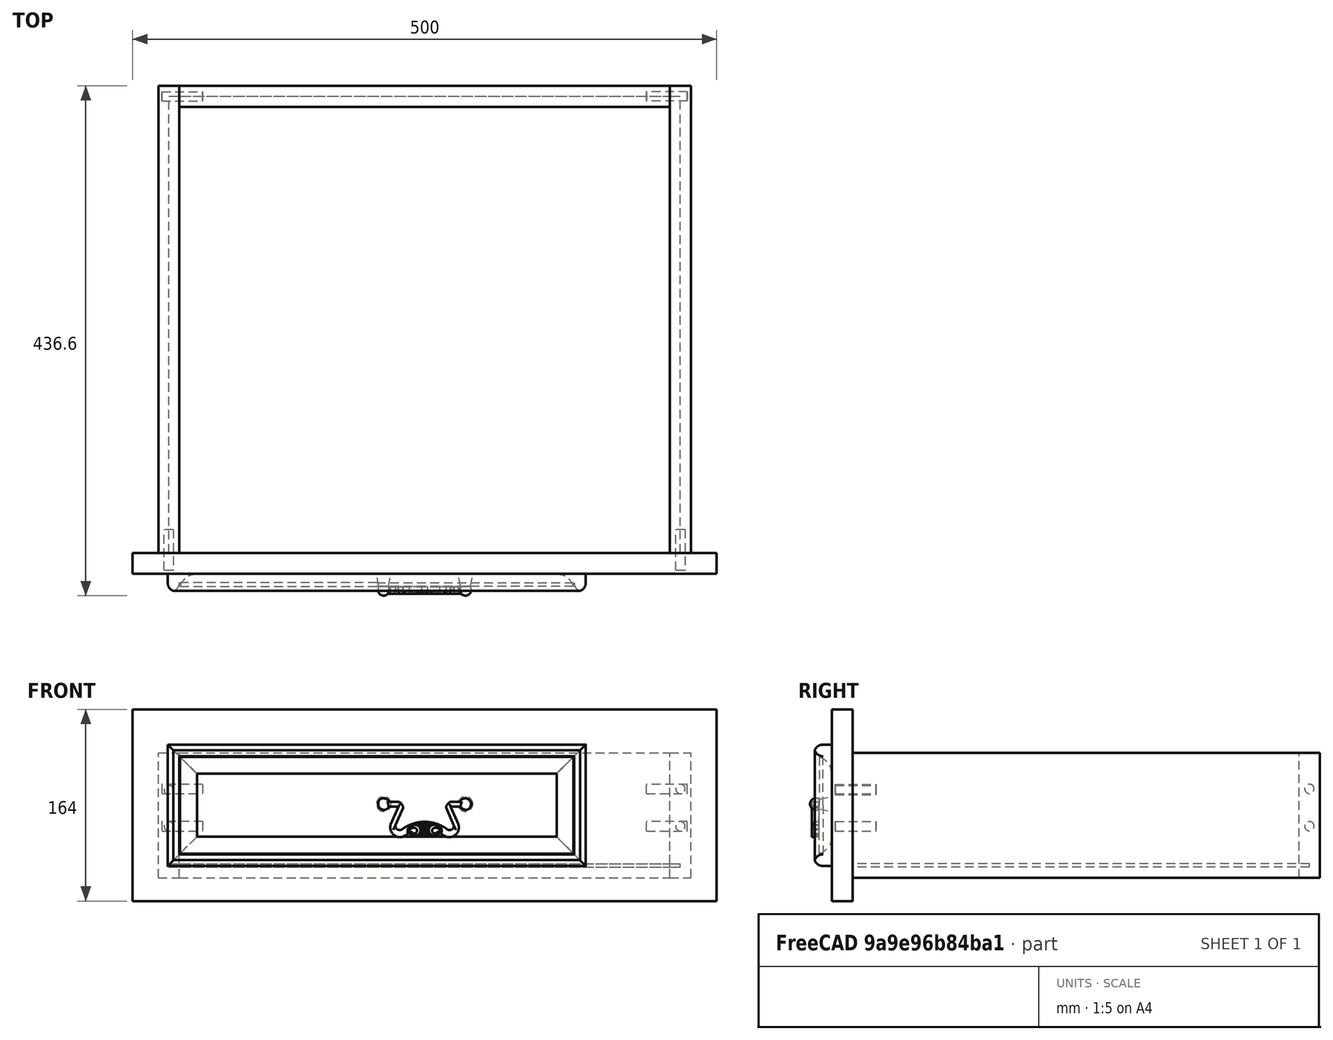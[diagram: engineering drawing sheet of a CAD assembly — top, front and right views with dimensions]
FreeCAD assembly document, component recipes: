
FREECAD ASSEMBLY — COMPONENT RECIPES ("msf058")

This assembly document has 8 components, labeled P0..P7 below (a component is one placed body or linked part). 5 of them carry a construction recipe — the FreeCAD feature program that regenerates the part from scratch, quoted from this document or its linked companion documents; the rest are supplied as boundary geometry only. No exploded tour is included for this assembly.
COMPONENT P0 — geometry summary ("Knife, Drawer Bottom HDF "; no construction recipe available for this part):
  bounding box: 438.0 x 391.0 x 3.0 mm
  tessellated surface: 12 triangles
  volume: 513774 mm^3 (100% of its bounding box)
  symmetry: 2-fold rotationally symmetric about the x axis; 2-fold rotationally symmetric about the y axis; 2-fold rotationally symmetric about the z axis; mirror-symmetric across its x mid-plane, y mid-plane, z mid-plane
COMPONENT P1 — geometry summary ("Knife, Drawer Bottom HDF 001"; no construction recipe available for this part):
  bounding box: 438.0 x 391.0 x 3.0 mm
  tessellated surface: 12 triangles
  volume: 513774 mm^3 (100% of its bounding box)
  symmetry: 2-fold rotationally symmetric about the x axis; 2-fold rotationally symmetric about the y axis; 2-fold rotationally symmetric about the z axis; mirror-symmetric across its x mid-plane, y mid-plane, z mid-plane
COMPONENT P2 — geometry summary ("Knife, Drawer Bottom HDF 002"; no construction recipe available for this part):
  bounding box: 438.0 x 391.0 x 3.0 mm
  tessellated surface: 12 triangles
  volume: 513774 mm^3 (100% of its bounding box)
  symmetry: 2-fold rotationally symmetric about the x axis; 2-fold rotationally symmetric about the y axis; 2-fold rotationally symmetric about the z axis; mirror-symmetric across its x mid-plane, y mid-plane, z mid-plane
COMPONENT P3 — recipe-attached ("Handle", modeled in this document).
Construction recipe (the document's own serialized feature program — sketch geometry with constraints, then the solid features built on it; lengths are millimeters unless a unit is written):

FEATURE [Sketcher::SketchObject] Sketch
  ArcFitTolerance = 0
  ExternalTypes = [0]
  FullyConstrained = true
  MakeInternals = false
  MapMode = 5
  _ExternalGeoVersion = 0
  sketch-geometry (24):
    g0: LineSegment StartX=-32 StartY=1.78 StartZ=0 EndX=-32 EndY=-2.22 EndZ=0
    g1: LineSegment StartX=-32 StartY=-2.22 StartZ=0 EndX=-23.78 EndY=-2.22 EndZ=0
    g2: ArcOfCircle CenterX=-23.78 CenterY=-3.3 CenterZ=0 NormalX=0 NormalY=0 NormalZ=1 AngleXU=0 Radius=1.08 StartAngle=-1.8e-15 EndAngle=1.5708
    g3: LineSegment StartX=-22.7 StartY=-3.3 StartZ=0 EndX=-29 EndY=-17.5 EndZ=0
    g4: ArcOfCircle CenterX=-21 CenterY=-20 CenterZ=0 NormalX=0 NormalY=0 NormalZ=1 AngleXU=0 Radius=8.38153 StartAngle=2.83871 EndAngle=5.01527
    g5: LineSegment StartX=-18.5 StartY=-28 StartZ=0 EndX=-13 EndY=-24.9433 EndZ=0
    g6: ArcOfCircle CenterX=-7.3 CenterY=-21 CenterZ=0 NormalX=0 NormalY=0 NormalZ=1 AngleXU=0 Radius=6.93109 StartAngle=3.7468 EndAngle=5.47738
    g7: ArcOfCircle CenterX=9e-16 CenterY=-20 CenterZ=0 NormalX=0 NormalY=0 NormalZ=1 AngleXU=0 Radius=6.5 StartAngle=4.3176 EndAngle=5.10718
    g8: ArcOfCircle CenterX=7.3 CenterY=-21 CenterZ=0 NormalX=0 NormalY=0 NormalZ=1 AngleXU=0 Radius=6.93109 StartAngle=3.9474 EndAngle=5.67797
    g9: LineSegment StartX=13 StartY=-24.9433 StartZ=0 EndX=18.5 EndY=-28 EndZ=0
    g10: ArcOfCircle CenterX=21 CenterY=-20 CenterZ=0 NormalX=0 NormalY=0 NormalZ=1 AngleXU=0 Radius=8.38153 StartAngle=4.4095 EndAngle=6.58607
    g11: LineSegment StartX=29 StartY=-17.5 StartZ=0 EndX=22.7 EndY=-3.3 EndZ=0
    g12: ArcOfCircle CenterX=23.78 CenterY=-3.3 CenterZ=0 NormalX=0 NormalY=0 NormalZ=1 AngleXU=0 Radius=1.08 StartAngle=1.5708 EndAngle=3.14159
    g13: LineSegment StartX=23.78 StartY=-2.22 StartZ=0 EndX=32 EndY=-2.22 EndZ=0
    g14: LineSegment StartX=32 StartY=-2.22 StartZ=0 EndX=32 EndY=1.78 EndZ=0
    g15: LineSegment StartX=32 StartY=1.78 StartZ=0 EndX=22.1 EndY=1.78 EndZ=0
    g16: ArcOfCircle CenterX=23.78 CenterY=-3.3 CenterZ=0 NormalX=0 NormalY=0 NormalZ=1 AngleXU=0 Radius=5.35059 StartAngle=1.89018 EndAngle=3.14159
    g17: LineSegment StartX=18.4294 StartY=-3.3 StartZ=0 EndX=25 EndY=-18 EndZ=0
    g18: ArcOfCircle CenterX=21.3162 CenterY=-18.56 CenterZ=0 NormalX=0 NormalY=0 NormalZ=1 AngleXU=0 Radius=3.72617 StartAngle=3.85555 EndAngle=6.43405
    g19: ArcOfCircle CenterX=-2e-15 CenterY=-48 CenterZ=0 NormalX=0 NormalY=0 NormalZ=1 AngleXU=0 Radius=32.73 StartAngle=0.970083 EndAngle=2.17151
    g20: ArcOfCircle CenterX=-21.3162 CenterY=-18.56 CenterZ=0 NormalX=0 NormalY=0 NormalZ=1 AngleXU=0 Radius=3.72617 StartAngle=2.99073 EndAngle=5.56923
    g21: LineSegment StartX=-25 StartY=-18 StartZ=0 EndX=-18.4294 EndY=-3.3 EndZ=0
    g22: ArcOfCircle CenterX=-23.78 CenterY=-3.3 CenterZ=0 NormalX=0 NormalY=0 NormalZ=1 AngleXU=0 Radius=5.35059 StartAngle=0 EndAngle=1.25141
    g23: LineSegment StartX=-22.1 StartY=1.78 StartZ=0 EndX=-32 EndY=1.78 EndZ=0
  constraints (71):
    c: Vertical(g0)
    c: Coincident(g0,g1)
    c: Horizontal(g1)
    c: Coincident(g2,g1)
    c: Coincident(g3,g2)
    c: Coincident(g4,g3)
    c: Coincident(g5,g4)
    c: Coincident(g6,g5)
    c: Coincident(g7,g6)
    c: Coincident(g8,g7)
    c: Coincident(g9,g8)
    c: Coincident(g10,g9)
    c: Coincident(g11,g10)
    c: Coincident(g12,g11)
    c: Coincident(g13,g12)
    c: Horizontal(g13)
    c: Coincident(g14,g13)
    c: Vertical(g14)
    c: Coincident(g15,g14)
    c: Horizontal(g15)
    c: Coincident(g16,g15)
    c: Coincident(g17,g16)
    c: Coincident(g18,g17)
    c: Coincident(g19,g18)
    c: Coincident(g20,g19)
    c: Coincident(g21,g20)
    c: Coincident(g22,g21)
    c: Coincident(g23,g22)
    c: Coincident(g23,g0)
    c: Horizontal(g18,g19)
    c: Symmetric(g6,g8,g-2)
    c: Symmetric(g5,g8,g-2)
    c: Symmetric(g20,g17,g-2)
    c: Symmetric(g3,g10,g-2)
    c: Symmetric(g0,g14,g-2)
    c: Symmetric(g22,g15,g-2)
    c: Symmetric(g1,g12,g-2)
    c: Symmetric(g16,g21,g-2)
    c: Symmetric(g2,g11,g-2)
    c: Symmetric(g4,g9,g-2)
    c: Symmetric(g20,g18,g-2)
    c: DistanceX(g14) = 32
    c: DistanceX(g15,g15) = 9.9
    c: DistanceX(g-1,g9) = 18.5
    c: DistanceX(g6,g-1) = 2.5
    c: DistanceX(g6,g-1) = 7.3
    c: DistanceX(g5,g-1) = 13
    c: DistanceX(g19,g-1) = 18.5
    c: DistanceX(g3,g-1) = 29
    c: DistanceX(g20,g-1) = 25
    c: DistanceY(g7,g-1) = 26
    c: DistanceY(g7,g-1) = 20
    c: Horizontal(g7,g6)
    c: DistanceY(g6,g-1) = 21
    c: DistanceY(g4,g-1) = 20
    c: DistanceY(g20,g-1) = 18.56
    c: DistanceX(g4,g-1) = 21
    c: DistanceY(g10,g-1) = 17.5
    c: DistanceY(g17,g-1) = 18
    c: Horizontal(g10,g4)
    c: Coincident(g16,g12)
    c: Coincident(g22,g2)
    c: DistanceY(g2,g-1) = 3.3
    c: DistanceX(g2,g-1) = 23.78
    c: Vertical(g12,g12)
    c: Horizontal(g11,g12)
    c: DistanceY(g2,g1) = 1.08
    c: DistanceY(g14,g14) = 4
    c: Horizontal(g2,g21)
    c: DistanceY(g19,g-1) = 21
    c: DistanceY(g19,g-1) = 48
FEATURE [PartDesign::Pad] Pad
  Direction = (0,0,1)
  Length = 6
  Length2 = 10
  Profile = -> Sketch
  ReferenceAxis = -> Sketch [N_Axis]
  SideType = 0
  Suppressed = false
  Type = 0
  Type2 = 0
FEATURE [Sketcher::SketchObject] Sketch001
  ArcFitTolerance = 0
  AttachmentOffset = pos=(0,3,3) rot=(0,0,1;4.71239rad)
  ExternalTypes = [0]
  FullyConstrained = true
  MakeInternals = false
  MapMode = 5
  Placement = pos=(35,0,3) rot=(0,1,0;1.5708rad)
  _ExternalGeoVersion = 0
  sketch-geometry (4):
    g0: ArcOfCircle CenterX=-0.404329 CenterY=0 CenterZ=0 NormalX=0 NormalY=0 NormalZ=1 AngleXU=0 Radius=5.02433 StartAngle=4.10302 EndAngle=6.28319
    g1: LineSegment StartX=-3.28 StartY=-4.12 StartZ=0 EndX=-14.06 EndY=-6.34 EndZ=0
    g2: LineSegment StartX=-14.06 StartY=-6.34 StartZ=0 EndX=-14.06 EndY=0 EndZ=0
    g3: LineSegment StartX=-14.06 StartY=0 StartZ=0 EndX=4.62 EndY=-1.2e-15 EndZ=0
  constraints (13):
    c: PointOnObject(g0,g-1)
    c: Coincident(g1,g0)
    c: Coincident(g2,g1)
    c: PointOnObject(g2,g-1)
    c: Vertical(g2)
    c: Coincident(g3,g2)
    c: Coincident(g3,g0)
    c: DistanceY(g2,g2) = 6.34
    c: PointOnObject(g0,g3)
    c: DistanceX(g-1,g0) = 4.62
    c: DistanceX(g0,g-1) = 3.28
    c: DistanceY(g0,g-1) = 4.12
    c: DistanceX(g1,g-1) = 14.06
FEATURE [PartDesign::Revolution] Revolution
  Angle = 360
  Angle2 = 0
  Axis = (2e-16,0,-1)
  Base = (35,0,3)
  BaseFeature = -> Pad
  FuseOrder = 0
  Profile = -> Sketch001
  ReferenceAxis = -> Sketch001 [H_Axis]
  Reversed = true
  Suppressed = false
  Type = 0
FEATURE [PartDesign::Mirrored] Mirrored
  MirrorPlane = -> YZ_Plane001
  Suppressed = false
  TransformMode = 0
FEATURE [PartDesign::MultiTransform] MultiTransform
  BaseFeature = -> Revolution
  Originals = -> [Revolution]
  Suppressed = false
  TransformMode = 0
  Transformations = -> [Mirrored]
FEATURE [Sketcher::SketchObject] Sketch002
  ArcFitTolerance = 0
  ExternalTypes = [0]
  FullyConstrained = false
  MakeInternals = false
  MapMode = 5
  Placement = pos=(0,0,0) rot=(1,0,0;3.14159rad)
  _ExternalGeoVersion = 0
  sketch-geometry (6):
    g0: ArcOfCircle CenterX=8.37325 CenterY=23.2848 CenterZ=0 NormalX=0 NormalY=0 NormalZ=1 AngleXU=0 Radius=5.42921 StartAngle=4.33984 EndAngle=6.97405
    g1: ArcOfCircle CenterX=7.9611 CenterY=22.3638 CenterZ=0 NormalX=0 NormalY=0 NormalZ=1 AngleXU=0 Radius=4.42164 StartAngle=0.796764 EndAngle=4.35084
    g2: ArcOfCircle CenterX=8.91823 CenterY=22.7616 CenterZ=0 NormalX=0 NormalY=0 NormalZ=1 AngleXU=0 Radius=2.4556 StartAngle=0.183027 EndAngle=3.90789
    g3: ArcOfCircle CenterX=9.44753 CenterY=23.8657 CenterZ=0 NormalX=0 NormalY=0 NormalZ=1 AngleXU=0 Radius=3.62796 StartAngle=4.02624 EndAngle=7.06929
    g4: LineSegment StartX=11.3328 StartY=23.2085 StartZ=0 EndX=11.0519 EndY=25.5257 EndZ=0
    g5: LineSegment StartX=12.0111 StartY=26.4328 StartZ=0 EndX=12.5575 EndY=26.7442 EndZ=0
  constraints (6):
    c: Coincident(g1,g0)
    c: Coincident(g3,g2)
    c: Coincident(g4,g2)
    c: Coincident(g4,g1)
    c: Coincident(g5,g3)
    c: Coincident(g5,g0)
FEATURE [PartDesign::Pocket] Pocket
  BaseFeature = -> MultiTransform
  Direction = (0,1e-16,1)
  Length = 1
  Length2 = 5
  Profile = -> Sketch002
  ReferenceAxis = -> Sketch002 [N_Axis]
  SideType = 0
  Suppressed = false
  Type = 0
  Type2 = 0
FEATURE [Sketcher::SketchObject] Sketch003
  ArcFitTolerance = 0
  ExternalTypes = [0]
  FullyConstrained = false
  MakeInternals = false
  MapMode = 5
  Placement = pos=(0,0,0) rot=(1,0,0;3.14159rad)
  _ExternalGeoVersion = 0
  sketch-geometry (4):
    g0: ArcOfCircle CenterX=8.78863 CenterY=22.2095 CenterZ=0 NormalX=0 NormalY=0 NormalZ=1 AngleXU=0 Radius=6.37434 StartAngle=1.16895 EndAngle=5.27179
    g1: ArcOfCircle CenterX=8.78863 CenterY=22.2095 CenterZ=0 NormalX=0 NormalY=0 NormalZ=1 AngleXU=0 Radius=7.27003 StartAngle=1.46029 EndAngle=5.028
    g2: LineSegment StartX=9.59035 StartY=29.4352 StartZ=0 EndX=11.2818 EndY=28.0761 EndZ=0
    g3: LineSegment StartX=11.0452 StartY=15.2986 StartZ=0 EndX=12.1714 EndY=16.8068 EndZ=0
  constraints (5):
    c: Coincident(g2,g1)
    c: Coincident(g2,g0)
    c: Coincident(g3,g1)
    c: Coincident(g3,g0)
    c: Coincident(g0,g1)
FEATURE [PartDesign::Pocket] Pocket001
  BaseFeature = -> Pocket
  Direction = (0,1e-16,1)
  Length = 1
  Length2 = 5
  Profile = -> Sketch003
  ReferenceAxis = -> Sketch003 [N_Axis]
  SideType = 0
  Suppressed = false
  Type = 0
  Type2 = 0
FEATURE [Sketcher::SketchObject] Sketch004
  ArcFitTolerance = 0
  ExternalTypes = [0]
  FullyConstrained = false
  MakeInternals = false
  MapMode = 5
  Placement = pos=(0,0,0) rot=(1,0,0;3.14159rad)
  _ExternalGeoVersion = 0
  sketch-geometry (4):
    g0: LineSegment StartX=3.03254 StartY=13.6466 StartZ=0 EndX=0 EndY=19.9742 EndZ=0
    g1: LineSegment StartX=2.14295 StartY=13.4233 StartZ=0 EndX=0 EndY=18.4771 EndZ=0
    g2: LineSegment StartX=0 StartY=19.9742 StartZ=0 EndX=0 EndY=18.4771 EndZ=0
    g3: LineSegment StartX=2.14295 StartY=13.4233 StartZ=0 EndX=3.03254 EndY=13.6466 EndZ=0
  constraints (6):
    c: PointOnObject(g0,g-2)
    c: PointOnObject(g1,g-2)
    c: Coincident(g2,g0)
    c: Coincident(g2,g1)
    c: Coincident(g3,g1)
    c: Coincident(g3,g0)
FEATURE [PartDesign::Pocket] Pocket002
  BaseFeature = -> Pocket001
  Direction = (0,1e-16,1)
  Length = 1
  Length2 = 5
  Profile = -> Sketch004
  ReferenceAxis = -> Sketch004 [N_Axis]
  SideType = 0
  Suppressed = false
  Type = 0
  Type2 = 0
FEATURE [PartDesign::Mirrored] Mirrored001
  MirrorPlane = -> YZ_Plane001
  Suppressed = false
  TransformMode = 0
FEATURE [PartDesign::MultiTransform] MultiTransform001
  BaseFeature = -> Pocket002
  Originals = -> [Pocket,Pocket001,Pocket002]
  Suppressed = false
  TransformMode = 0
  Transformations = -> [Mirrored001]
FEATURE [PartDesign::Fillet] Fillet
  Base = -> MultiTransform001 [Edge104,Edge17,Edge4,Edge98]
  BaseFeature = -> MultiTransform001
  Radius = 3
  SupportTransform = false
  Suppressed = false
  UseAllEdges = false
FEATURE [PartDesign::Chamfer] Chamfer
  Angle = 45
  Base = -> Fillet [Edge101,Edge15,Edge129,Edge135,Edge143,Edge140,Edge132,Edge131]
  BaseFeature = -> Fillet
  ChamferType = 0
  FlipDirection = false
  Size = 0.8
  Size2 = 1
  SupportTransform = false
  Suppressed = false
  UseAllEdges = false
FEATURE [PartDesign::Fillet] Fillet001
  Base = -> Chamfer [Edge149,Edge12]
  BaseFeature = -> Chamfer
  Radius = 0.2
  SupportTransform = false
  Suppressed = false
  UseAllEdges = false
FEATURE [PartDesign::Body] Body
  AllowCompound = true
  Group = -> [Sketch,Pad,Sketch001,Revolution,MultiTransform,Mirrored,Sketch002,Pocket,Sketch003,Pocket001,Sketch004,Pocket002,MultiTransform001,Mirrored001,Fillet,Chamfer,Fillet001]
  Origin = -> Origin001
  Placement = pos=(241,-34.9822,76.0422) rot=(0,0.707107,0.707107;3.14159rad)
  Tip = -> Fillet001
COMPONENT P4 — recipe-attached ("Decoration Left", modeled in this document).
Construction recipe (the document's own serialized feature program — sketch geometry with constraints, then the solid features built on it; lengths are millimeters unless a unit is written):

FEATURE [Sketcher::SketchObject] Sketch005  label="Pattern, Frame"
  ArcFitTolerance = 0
  AttachmentOffset = pos=(21,23,33) rot=(0,1,0;0rad)
  ExternalTypes = [0]
  FullyConstrained = true
  MakeInternals = false
  MapMode = 5
  Placement = pos=(21,-33,23) rot=(1,0,0;1.5708rad)
  _ExternalGeoVersion = 0
  sketch-geometry (4):
    g0: LineSegment StartX=0 StartY=104 StartZ=0 EndX=25 EndY=104 EndZ=0
    g1: LineSegment StartX=25 StartY=104 StartZ=0 EndX=25 EndY=0 EndZ=0
    g2: LineSegment StartX=25 StartY=0 StartZ=0 EndX=0 EndY=0 EndZ=0
    g3: LineSegment StartX=0 StartY=0 StartZ=0 EndX=0 EndY=104 EndZ=0
  constraints (11):
    c: Coincident(g0,g1)
    c: Coincident(g1,g2)
    c: Coincident(g2,g3)
    c: Coincident(g3,g0)
    c: Horizontal(g0)
    c: Horizontal(g2)
    c: Vertical(g1)
    c: Vertical(g3)
    c: Coincident(g2,g-1)
    c: DistanceX(g0,g0) = 25  'SizeX'
    c: DistanceY(g3,g3) = 104  'SizeY'
FEATURE [PartDesign::Pad] Pad001  label="Frame"
  Direction = (0,-1,2e-16)
  Length = 15
  Length2 = 10
  Placement = pos=(21,-33,23) rot=(1,0,0;1.5708rad)
  Profile = -> Sketch005
  Reversed = true
  SideType = 0
  Suppressed = false
  Type = 0
  Type2 = 0
FEATURE [PartDesign::Chamfer] Frame45Cut
  Angle = 45
  Base = -> Pad001 [Edge2,Edge5]
  BaseFeature = -> Pad001
  ChamferType = 0
  FlipDirection = false
  Placement = pos=(21,-33,23) rot=(1,0,0;1.5708rad)
  Size = 24.99
  Size2 = 1
  SupportTransform = false
  Suppressed = false
  UseAllEdges = false
FEATURE [Sketcher::SketchObject] routerPattern001
  ArcFitTolerance = 0
  ExternalTypes = [0]
  FullyConstrained = true
  MakeInternals = false
  Placement = pos=(46,-33,75) rot=(0,0,1;0rad)
  _ExternalGeoVersion = 0
  sketch-geometry (1):
    g0: Circle CenterX=0 CenterY=0 CenterZ=0 NormalX=0 NormalY=0 NormalZ=1 AngleXU=0 Radius=15
  constraints (2):
    c: Coincident(g0,g-1)
    c: Radius(g0) = 15
FEATURE [PartDesign::Pocket] router001  label="Cove 001"
  BaseFeature = -> Frame45Cut
  Direction = (0,0,-1)
  Length = 5
  Length2 = 5
  Placement = pos=(21,-33,23) rot=(1,0,0;1.5708rad)
  Profile = -> routerPattern001
  SideType = 2
  Suppressed = false
  Type = 1
  Type2 = 0
FEATURE [Sketcher::SketchObject] routerPattern005
  ArcFitTolerance = 0
  ExternalTypes = [0]
  FullyConstrained = true
  MakeInternals = false
  Placement = pos=(31,-33,75) rot=(0,0,1;0rad)
  _ExternalGeoVersion = 0
  sketch-geometry (4):
    g0: ArcOfCircle CenterX=7.50003 CenterY=-7.50003 CenterZ=0 NormalX=0 NormalY=0 NormalZ=1 AngleXU=0 Radius=7.50003 StartAngle=1.5708 EndAngle=3.14159
    g1: ArcOfCircle CenterX=-7.50003 CenterY=7.50003 CenterZ=0 NormalX=0 NormalY=0 NormalZ=1 AngleXU=0 Radius=7.50003 StartAngle=4.71239 EndAngle=6.28319
    g2: ArcOfCircle CenterX=7.50003 CenterY=7.50003 CenterZ=0 NormalX=0 NormalY=0 NormalZ=1 AngleXU=0 Radius=7.50003 StartAngle=3.14159 EndAngle=4.71239
    g3: ArcOfCircle CenterX=-7.50003 CenterY=-7.50003 CenterZ=0 NormalX=0 NormalY=0 NormalZ=1 AngleXU=0 Radius=7.50003 StartAngle=3.61945e-06 EndAngle=1.5708
  constraints (16):
    c: Equal(g3,g1)
    c: Equal(g1,g2)
    c: Equal(g2,g0)
    c: Vertical(g0,g2)
    c: Horizontal(g3,g0)
    c: Vertical(g1,g3)
    c: Horizontal(g1,g2)
    c: Coincident(g1,g2)
    c: Coincident(g0,g2)
    c: Coincident(g3,g0)
    c: Coincident(g3,g1)
    c: PointOnObject(g1,g-1)
    c: PointOnObject(g1,g-2)
    c: DistanceY(g0,g-1) = 7.5
    c: Vertical(g0,g0)
    c: Horizontal(g1,g1)
FEATURE [PartDesign::Pocket] router005  label="RoundOver2 001"
  BaseFeature = -> router001
  Direction = (0,0,-1)
  Length = 5
  Length2 = 5
  Placement = pos=(21,-33,23) rot=(1,0,0;1.5708rad)
  Profile = -> routerPattern005
  SideType = 2
  Suppressed = false
  Type = 1
  Type2 = 0
FEATURE [Sketcher::SketchObject] routerPattern008
  ArcFitTolerance = 0
  ExternalTypes = [0]
  FullyConstrained = true
  MakeInternals = false
  Placement = pos=(21,-33,75) rot=(0,0,1;0rad)
  _ExternalGeoVersion = 0
  sketch-geometry (4):
    g0: ArcOfCircle CenterX=7.50002 CenterY=-7.50002 CenterZ=0 NormalX=0 NormalY=0 NormalZ=1 AngleXU=0 Radius=7.50002 StartAngle=1.5708 EndAngle=3.14159
    g1: ArcOfCircle CenterX=-7.50002 CenterY=7.50002 CenterZ=0 NormalX=0 NormalY=0 NormalZ=1 AngleXU=0 Radius=7.50002 StartAngle=4.71239 EndAngle=6.28319
    g2: ArcOfCircle CenterX=7.50002 CenterY=7.50002 CenterZ=0 NormalX=0 NormalY=0 NormalZ=1 AngleXU=0 Radius=7.50002 StartAngle=3.14159 EndAngle=4.71239
    g3: ArcOfCircle CenterX=-7.50002 CenterY=-7.50002 CenterZ=0 NormalX=0 NormalY=0 NormalZ=1 AngleXU=0 Radius=7.50002 StartAngle=2.46945e-06 EndAngle=1.5708
  constraints (16):
    c: Equal(g3,g1)
    c: Equal(g1,g2)
    c: Equal(g2,g0)
    c: Vertical(g0,g2)
    c: Horizontal(g3,g0)
    c: Vertical(g1,g3)
    c: Horizontal(g1,g2)
    c: Coincident(g1,g2)
    c: Coincident(g0,g2)
    c: Coincident(g3,g0)
    c: Coincident(g3,g1)
    c: PointOnObject(g1,g-1)
    c: PointOnObject(g1,g-2)
    c: DistanceY(g0,g-1) = 7.5
    c: Vertical(g0,g0)
    c: Horizontal(g1,g1)
FEATURE [PartDesign::Pocket] router008  label="RoundOver2 004"
  BaseFeature = -> router005
  Direction = (0,0,-1)
  Length = 5
  Length2 = 5
  Placement = pos=(21,-33,23) rot=(1,0,0;1.5708rad)
  Profile = -> routerPattern008
  SideType = 2
  Suppressed = false
  Type = 1
  Type2 = 0
FEATURE [PartDesign::Body] Body001  label="Body, Frame"
  AllowCompound = true
  Group = -> [Sketch005,Pad001,Frame45Cut,routerPattern001,router001,routerPattern005,router005,routerPattern008,router008]
  Origin = -> Origin003
  Tip = -> router008
COMPONENT P5 — recipe-attached ("Decoration Top", modeled in this document).
Construction recipe (the document's own serialized feature program — sketch geometry with constraints, then the solid features built on it; lengths are millimeters unless a unit is written):

FEATURE [Sketcher::SketchObject] Sketch006  label="Pattern, Frame001"
  ArcFitTolerance = 0
  AttachmentOffset = pos=(21,102,33) rot=(0,1,0;0rad)
  ExternalTypes = [0]
  FullyConstrained = true
  MakeInternals = false
  MapMode = 5
  Placement = pos=(21,-33,102) rot=(1,0,0;1.5708rad)
  _ExternalGeoVersion = 0
  sketch-geometry (4):
    g0: LineSegment StartX=0 StartY=25 StartZ=0 EndX=358 EndY=25 EndZ=0
    g1: LineSegment StartX=358 StartY=25 StartZ=0 EndX=358 EndY=0 EndZ=0
    g2: LineSegment StartX=358 StartY=0 StartZ=0 EndX=0 EndY=0 EndZ=0
    g3: LineSegment StartX=0 StartY=0 StartZ=0 EndX=0 EndY=25 EndZ=0
  constraints (11):
    c: Coincident(g0,g1)
    c: Coincident(g1,g2)
    c: Coincident(g2,g3)
    c: Coincident(g3,g0)
    c: Horizontal(g0)
    c: Horizontal(g2)
    c: Vertical(g1)
    c: Vertical(g3)
    c: Coincident(g2,g-1)
    c: DistanceX(g0,g0) = 358  'SizeX'
    c: DistanceY(g3,g3) = 25  'SizeY'
FEATURE [PartDesign::Pad] Pad002  label="Frame001"
  Direction = (0,-1,2e-16)
  Length = 15
  Length2 = 10
  Placement = pos=(21,-33,102) rot=(1,0,0;1.5708rad)
  Profile = -> Sketch006
  Reversed = true
  SideType = 0
  Suppressed = false
  Type = 0
  Type2 = 0
FEATURE [PartDesign::Chamfer] Frame45Cut001
  Angle = 45
  Base = -> Pad002 [Edge8,Edge5]
  BaseFeature = -> Pad002
  ChamferType = 0
  FlipDirection = false
  Placement = pos=(21,-33,102) rot=(1,0,0;1.5708rad)
  Size = 24.99
  Size2 = 1
  SupportTransform = false
  Suppressed = false
  UseAllEdges = false
FEATURE [Sketcher::SketchObject] routerPattern002
  ArcFitTolerance = 0
  ExternalTypes = [0]
  FullyConstrained = true
  MakeInternals = false
  Placement = pos=(200,-33,102) rot=(0,1,0;1.5708rad)
  _ExternalGeoVersion = 0
  sketch-geometry (1):
    g0: Circle CenterX=0 CenterY=0 CenterZ=0 NormalX=0 NormalY=0 NormalZ=1 AngleXU=0 Radius=15
  constraints (2):
    c: Coincident(g0,g-1)
    c: Radius(g0) = 15
FEATURE [PartDesign::Pocket] router002  label="Cove 002"
  BaseFeature = -> Frame45Cut001
  Direction = (-1,0,-2e-16)
  Length = 5
  Length2 = 5
  Placement = pos=(21,-33,102) rot=(1,0,0;1.5708rad)
  Profile = -> routerPattern002
  SideType = 2
  Suppressed = false
  Type = 1
  Type2 = 0
FEATURE [Sketcher::SketchObject] routerPattern006
  ArcFitTolerance = 0
  ExternalTypes = [0]
  FullyConstrained = true
  MakeInternals = false
  Placement = pos=(200,-33,117) rot=(0,1,0;1.5708rad)
  _ExternalGeoVersion = 0
  sketch-geometry (4):
    g0: ArcOfCircle CenterX=7.50002 CenterY=-7.50002 CenterZ=0 NormalX=0 NormalY=0 NormalZ=1 AngleXU=0 Radius=7.50002 StartAngle=1.5708 EndAngle=3.14159
    g1: ArcOfCircle CenterX=-7.50002 CenterY=7.50002 CenterZ=0 NormalX=0 NormalY=0 NormalZ=1 AngleXU=0 Radius=7.50002 StartAngle=4.71239 EndAngle=6.28319
    g2: ArcOfCircle CenterX=7.50002 CenterY=7.50002 CenterZ=0 NormalX=0 NormalY=0 NormalZ=1 AngleXU=0 Radius=7.50002 StartAngle=3.14159 EndAngle=4.71239
    g3: ArcOfCircle CenterX=-7.50002 CenterY=-7.50002 CenterZ=0 NormalX=0 NormalY=0 NormalZ=1 AngleXU=0 Radius=7.50002 StartAngle=2.36025e-06 EndAngle=1.5708
  constraints (16):
    c: Equal(g3,g1)
    c: Equal(g1,g2)
    c: Equal(g2,g0)
    c: Vertical(g0,g2)
    c: Horizontal(g3,g0)
    c: Vertical(g1,g3)
    c: Horizontal(g1,g2)
    c: Coincident(g1,g2)
    c: Coincident(g0,g2)
    c: Coincident(g3,g0)
    c: Coincident(g3,g1)
    c: PointOnObject(g1,g-1)
    c: PointOnObject(g1,g-2)
    c: DistanceY(g0,g-1) = 7.5
    c: Vertical(g0,g0)
    c: Horizontal(g1,g1)
FEATURE [PartDesign::Pocket] router006  label="RoundOver2 002"
  BaseFeature = -> router002
  Direction = (-1,0,-2e-16)
  Length = 5
  Length2 = 5
  Placement = pos=(21,-33,102) rot=(1,0,0;1.5708rad)
  Profile = -> routerPattern006
  SideType = 2
  Suppressed = false
  Type = 1
  Type2 = 0
FEATURE [Sketcher::SketchObject] routerPattern009
  ArcFitTolerance = 0
  ExternalTypes = [0]
  FullyConstrained = true
  MakeInternals = false
  Placement = pos=(200,-33,127) rot=(0,1,0;1.5708rad)
  _ExternalGeoVersion = 0
  sketch-geometry (4):
    g0: ArcOfCircle CenterX=7.50002 CenterY=-7.50002 CenterZ=0 NormalX=0 NormalY=0 NormalZ=1 AngleXU=0 Radius=7.50002 StartAngle=1.5708 EndAngle=3.14159
    g1: ArcOfCircle CenterX=-7.50002 CenterY=7.50002 CenterZ=0 NormalX=0 NormalY=0 NormalZ=1 AngleXU=0 Radius=7.50002 StartAngle=4.71239 EndAngle=6.28319
    g2: ArcOfCircle CenterX=7.50002 CenterY=7.50002 CenterZ=0 NormalX=0 NormalY=0 NormalZ=1 AngleXU=0 Radius=7.50002 StartAngle=3.14159 EndAngle=4.71239
    g3: ArcOfCircle CenterX=-7.50002 CenterY=-7.50002 CenterZ=0 NormalX=0 NormalY=0 NormalZ=1 AngleXU=0 Radius=7.50002 StartAngle=2.23483e-06 EndAngle=1.5708
  constraints (16):
    c: Equal(g3,g1)
    c: Equal(g1,g2)
    c: Equal(g2,g0)
    c: Vertical(g0,g2)
    c: Horizontal(g3,g0)
    c: Vertical(g1,g3)
    c: Horizontal(g1,g2)
    c: Coincident(g1,g2)
    c: Coincident(g0,g2)
    c: Coincident(g3,g0)
    c: Coincident(g3,g1)
    c: PointOnObject(g1,g-1)
    c: PointOnObject(g1,g-2)
    c: DistanceY(g0,g-1) = 7.5
    c: Vertical(g0,g0)
    c: Horizontal(g1,g1)
FEATURE [PartDesign::Pocket] router009  label="RoundOver2 005"
  BaseFeature = -> router006
  Direction = (-1,0,-2e-16)
  Length = 5
  Length2 = 5
  Placement = pos=(21,-33,102) rot=(1,0,0;1.5708rad)
  Profile = -> routerPattern009
  SideType = 2
  Suppressed = false
  Type = 1
  Type2 = 0
FEATURE [PartDesign::Body] Body002  label="Body, Frame001"
  AllowCompound = true
  Group = -> [Sketch006,Pad002,Frame45Cut001,routerPattern002,router002,routerPattern006,router006,routerPattern009,router009]
  Origin = -> Origin005
  Tip = -> router009
COMPONENT P6 — recipe-attached ("Decoration Right", modeled in this document).
Construction recipe (the document's own serialized feature program — sketch geometry with constraints, then the solid features built on it; lengths are millimeters unless a unit is written):

FEATURE [Sketcher::SketchObject] Sketch007  label="Pattern, Frame002"
  ArcFitTolerance = 0
  AttachmentOffset = pos=(354,23,33) rot=(0,1,0;0rad)
  ExternalTypes = [0]
  FullyConstrained = true
  MakeInternals = false
  MapMode = 5
  Placement = pos=(354,-33,23) rot=(1,0,0;1.5708rad)
  _ExternalGeoVersion = 0
  sketch-geometry (4):
    g0: LineSegment StartX=0 StartY=104 StartZ=0 EndX=25 EndY=104 EndZ=0
    g1: LineSegment StartX=25 StartY=104 StartZ=0 EndX=25 EndY=0 EndZ=0
    g2: LineSegment StartX=25 StartY=0 StartZ=0 EndX=0 EndY=0 EndZ=0
    g3: LineSegment StartX=0 StartY=0 StartZ=0 EndX=0 EndY=104 EndZ=0
  constraints (11):
    c: Coincident(g0,g1)
    c: Coincident(g1,g2)
    c: Coincident(g2,g3)
    c: Coincident(g3,g0)
    c: Horizontal(g0)
    c: Horizontal(g2)
    c: Vertical(g1)
    c: Vertical(g3)
    c: Coincident(g2,g-1)
    c: DistanceX(g0,g0) = 25  'SizeX'
    c: DistanceY(g3,g3) = 104  'SizeY'
FEATURE [PartDesign::Pad] Pad003  label="Frame002"
  Direction = (0,-1,2e-16)
  Length = 15
  Length2 = 10
  Placement = pos=(354,-33,23) rot=(1,0,0;1.5708rad)
  Profile = -> Sketch007
  Reversed = true
  SideType = 0
  Suppressed = false
  Type = 0
  Type2 = 0
FEATURE [PartDesign::Chamfer] Frame45Cut002
  Angle = 45
  Base = -> Pad003 [Edge1,Edge8]
  BaseFeature = -> Pad003
  ChamferType = 0
  FlipDirection = false
  Placement = pos=(354,-33,23) rot=(1,0,0;1.5708rad)
  Size = 24.99
  Size2 = 1
  SupportTransform = false
  Suppressed = false
  UseAllEdges = false
FEATURE [Sketcher::SketchObject] routerPattern003
  ArcFitTolerance = 0
  ExternalTypes = [0]
  FullyConstrained = true
  MakeInternals = false
  Placement = pos=(354,-33,75) rot=(0,0,1;0rad)
  _ExternalGeoVersion = 0
  sketch-geometry (1):
    g0: Circle CenterX=0 CenterY=0 CenterZ=0 NormalX=0 NormalY=0 NormalZ=1 AngleXU=0 Radius=15
  constraints (2):
    c: Coincident(g0,g-1)
    c: Radius(g0) = 15
FEATURE [PartDesign::Pocket] router003  label="Cove 003"
  BaseFeature = -> Frame45Cut002
  Direction = (0,0,-1)
  Length = 5
  Length2 = 5
  Placement = pos=(354,-33,23) rot=(1,0,0;1.5708rad)
  Profile = -> routerPattern003
  SideType = 2
  Suppressed = false
  Type = 1
  Type2 = 0
FEATURE [Sketcher::SketchObject] routerPattern007
  ArcFitTolerance = 0
  ExternalTypes = [0]
  FullyConstrained = true
  MakeInternals = false
  Placement = pos=(369,-33,75) rot=(0,0,1;0rad)
  _ExternalGeoVersion = 0
  sketch-geometry (4):
    g0: ArcOfCircle CenterX=7.50003 CenterY=-7.50003 CenterZ=0 NormalX=0 NormalY=0 NormalZ=1 AngleXU=0 Radius=7.50003 StartAngle=1.5708 EndAngle=3.14159
    g1: ArcOfCircle CenterX=-7.50003 CenterY=7.50003 CenterZ=0 NormalX=0 NormalY=0 NormalZ=1 AngleXU=0 Radius=7.50003 StartAngle=4.71239 EndAngle=6.28319
    g2: ArcOfCircle CenterX=7.50003 CenterY=7.50003 CenterZ=0 NormalX=0 NormalY=0 NormalZ=1 AngleXU=0 Radius=7.50003 StartAngle=3.14159 EndAngle=4.71239
    g3: ArcOfCircle CenterX=-7.50003 CenterY=-7.50003 CenterZ=0 NormalX=0 NormalY=0 NormalZ=1 AngleXU=0 Radius=7.50003 StartAngle=3.36109e-06 EndAngle=1.5708
  constraints (16):
    c: Equal(g3,g1)
    c: Equal(g1,g2)
    c: Equal(g2,g0)
    c: Vertical(g0,g2)
    c: Horizontal(g3,g0)
    c: Vertical(g1,g3)
    c: Horizontal(g1,g2)
    c: Coincident(g1,g2)
    c: Coincident(g0,g2)
    c: Coincident(g3,g0)
    c: Coincident(g3,g1)
    c: PointOnObject(g1,g-1)
    c: PointOnObject(g1,g-2)
    c: DistanceY(g0,g-1) = 7.5
    c: Vertical(g0,g0)
    c: Horizontal(g1,g1)
FEATURE [PartDesign::Pocket] router007  label="RoundOver2 003"
  BaseFeature = -> router003
  Direction = (0,0,-1)
  Length = 5
  Length2 = 5
  Placement = pos=(354,-33,23) rot=(1,0,0;1.5708rad)
  Profile = -> routerPattern007
  SideType = 2
  Suppressed = false
  Type = 1
  Type2 = 0
FEATURE [Sketcher::SketchObject] routerPattern011
  ArcFitTolerance = 0
  ExternalTypes = [0]
  FullyConstrained = true
  MakeInternals = false
  Placement = pos=(379,-33,75) rot=(0,0,1;0rad)
  _ExternalGeoVersion = 0
  sketch-geometry (4):
    g0: ArcOfCircle CenterX=7.50002 CenterY=-7.50002 CenterZ=0 NormalX=0 NormalY=0 NormalZ=1 AngleXU=0 Radius=7.50002 StartAngle=1.5708 EndAngle=3.14159
    g1: ArcOfCircle CenterX=-7.50002 CenterY=7.50002 CenterZ=0 NormalX=0 NormalY=0 NormalZ=1 AngleXU=0 Radius=7.50002 StartAngle=4.71239 EndAngle=6.28319
    g2: ArcOfCircle CenterX=7.50002 CenterY=7.50002 CenterZ=0 NormalX=0 NormalY=0 NormalZ=1 AngleXU=0 Radius=7.50002 StartAngle=3.14159 EndAngle=4.71239
    g3: ArcOfCircle CenterX=-7.50002 CenterY=-7.50002 CenterZ=0 NormalX=0 NormalY=0 NormalZ=1 AngleXU=0 Radius=7.50002 StartAngle=2.68196e-06 EndAngle=1.5708
  constraints (16):
    c: Equal(g3,g1)
    c: Equal(g1,g2)
    c: Equal(g2,g0)
    c: Vertical(g0,g2)
    c: Horizontal(g3,g0)
    c: Vertical(g1,g3)
    c: Horizontal(g1,g2)
    c: Coincident(g1,g2)
    c: Coincident(g0,g2)
    c: Coincident(g3,g0)
    c: Coincident(g3,g1)
    c: PointOnObject(g1,g-1)
    c: PointOnObject(g1,g-2)
    c: DistanceY(g0,g-1) = 7.5
    c: Vertical(g0,g0)
    c: Horizontal(g1,g1)
FEATURE [PartDesign::Pocket] router011  label="RoundOver2 007"
  BaseFeature = -> router007
  Direction = (0,0,-1)
  Length = 5
  Length2 = 5
  Placement = pos=(354,-33,23) rot=(1,0,0;1.5708rad)
  Profile = -> routerPattern011
  SideType = 2
  Suppressed = false
  Type = 1
  Type2 = 0
FEATURE [PartDesign::Body] Body003  label="Body, Frame002"
  AllowCompound = true
  Group = -> [Sketch007,Pad003,Frame45Cut002,routerPattern003,router003,routerPattern007,router007,routerPattern011,router011]
  Origin = -> Origin007
  Tip = -> router011
COMPONENT P7 — recipe-attached ("Decoration Bottom", modeled in this document).
Construction recipe (the document's own serialized feature program — sketch geometry with constraints, then the solid features built on it; lengths are millimeters unless a unit is written):

FEATURE [Sketcher::SketchObject] Sketch008  label="Pattern, Frame003"
  ArcFitTolerance = 0
  AttachmentOffset = pos=(21,23,33) rot=(0,1,0;0rad)
  ExternalTypes = [0]
  FullyConstrained = true
  MakeInternals = false
  MapMode = 5
  Placement = pos=(21,-33,23) rot=(1,0,0;1.5708rad)
  _ExternalGeoVersion = 0
  sketch-geometry (4):
    g0: LineSegment StartX=0 StartY=25 StartZ=0 EndX=358 EndY=25 EndZ=0
    g1: LineSegment StartX=358 StartY=25 StartZ=0 EndX=358 EndY=0 EndZ=0
    g2: LineSegment StartX=358 StartY=0 StartZ=0 EndX=0 EndY=0 EndZ=0
    g3: LineSegment StartX=0 StartY=0 StartZ=0 EndX=0 EndY=25 EndZ=0
  constraints (11):
    c: Coincident(g0,g1)
    c: Coincident(g1,g2)
    c: Coincident(g2,g3)
    c: Coincident(g3,g0)
    c: Horizontal(g0)
    c: Horizontal(g2)
    c: Vertical(g1)
    c: Vertical(g3)
    c: Coincident(g2,g-1)
    c: DistanceX(g0,g0) = 358  'SizeX'
    c: DistanceY(g3,g3) = 25  'SizeY'
FEATURE [PartDesign::Pad] Pad004  label="Frame003"
  Direction = (0,-1,2e-16)
  Length = 15
  Length2 = 10
  Placement = pos=(21,-33,23) rot=(1,0,0;1.5708rad)
  Profile = -> Sketch008
  Reversed = true
  SideType = 0
  Suppressed = false
  Type = 0
  Type2 = 0
FEATURE [PartDesign::Chamfer] Frame45Cut003
  Angle = 45
  Base = -> Pad004 [Edge1,Edge2]
  BaseFeature = -> Pad004
  ChamferType = 0
  FlipDirection = false
  Placement = pos=(21,-33,23) rot=(1,0,0;1.5708rad)
  Size = 24.99
  Size2 = 1
  SupportTransform = false
  Suppressed = false
  UseAllEdges = false
FEATURE [Sketcher::SketchObject] routerPattern
  ArcFitTolerance = 0
  ExternalTypes = [0]
  FullyConstrained = true
  MakeInternals = false
  Placement = pos=(200,-33,48) rot=(0,1,0;1.5708rad)
  _ExternalGeoVersion = 0
  sketch-geometry (1):
    g0: Circle CenterX=0 CenterY=0 CenterZ=0 NormalX=0 NormalY=0 NormalZ=1 AngleXU=0 Radius=15
  constraints (2):
    c: Coincident(g0,g-1)
    c: Radius(g0) = 15
FEATURE [PartDesign::Pocket] router  label="Cove "
  BaseFeature = -> Frame45Cut003
  Direction = (-1,0,-2e-16)
  Length = 5
  Length2 = 5
  Placement = pos=(21,-33,23) rot=(1,0,0;1.5708rad)
  Profile = -> routerPattern
  SideType = 2
  Suppressed = false
  Type = 1
  Type2 = 0
FEATURE [Sketcher::SketchObject] routerPattern004
  ArcFitTolerance = 0
  ExternalTypes = [0]
  FullyConstrained = true
  MakeInternals = false
  Placement = pos=(200,-33,33) rot=(0,1,0;1.5708rad)
  _ExternalGeoVersion = 0
  sketch-geometry (4):
    g0: ArcOfCircle CenterX=7.50002 CenterY=-7.50002 CenterZ=0 NormalX=0 NormalY=0 NormalZ=1 AngleXU=0 Radius=7.50002 StartAngle=1.5708 EndAngle=3.14159
    g1: ArcOfCircle CenterX=-7.50002 CenterY=7.50002 CenterZ=0 NormalX=0 NormalY=0 NormalZ=1 AngleXU=0 Radius=7.50002 StartAngle=4.71239 EndAngle=6.28319
    g2: ArcOfCircle CenterX=7.50002 CenterY=7.50002 CenterZ=0 NormalX=0 NormalY=0 NormalZ=1 AngleXU=0 Radius=7.50002 StartAngle=3.14159 EndAngle=4.71239
    g3: ArcOfCircle CenterX=-7.50002 CenterY=-7.50002 CenterZ=0 NormalX=0 NormalY=0 NormalZ=1 AngleXU=0 Radius=7.50002 StartAngle=2.17516e-06 EndAngle=1.5708
  constraints (16):
    c: Equal(g3,g1)
    c: Equal(g1,g2)
    c: Equal(g2,g0)
    c: Vertical(g0,g2)
    c: Horizontal(g3,g0)
    c: Vertical(g1,g3)
    c: Horizontal(g1,g2)
    c: Coincident(g1,g2)
    c: Coincident(g0,g2)
    c: Coincident(g3,g0)
    c: Coincident(g3,g1)
    c: PointOnObject(g1,g-1)
    c: PointOnObject(g1,g-2)
    c: DistanceY(g0,g-1) = 7.5
    c: Vertical(g0,g0)
    c: Horizontal(g1,g1)
FEATURE [PartDesign::Pocket] router004  label="RoundOver2 "
  BaseFeature = -> router
  Direction = (-1,0,-2e-16)
  Length = 5
  Length2 = 5
  Placement = pos=(21,-33,23) rot=(1,0,0;1.5708rad)
  Profile = -> routerPattern004
  SideType = 2
  Suppressed = false
  Type = 1
  Type2 = 0
FEATURE [Sketcher::SketchObject] routerPattern010
  ArcFitTolerance = 0
  ExternalTypes = [0]
  FullyConstrained = true
  MakeInternals = false
  Placement = pos=(200,-33,23) rot=(0,1,0;1.5708rad)
  _ExternalGeoVersion = 0
  sketch-geometry (4):
    g0: ArcOfCircle CenterX=7.50003 CenterY=-7.50003 CenterZ=0 NormalX=0 NormalY=0 NormalZ=1 AngleXU=0 Radius=7.50003 StartAngle=1.5708 EndAngle=3.14159
    g1: ArcOfCircle CenterX=-7.50003 CenterY=7.50003 CenterZ=0 NormalX=0 NormalY=0 NormalZ=1 AngleXU=0 Radius=7.50003 StartAngle=4.71239 EndAngle=6.28319
    g2: ArcOfCircle CenterX=7.50003 CenterY=7.50003 CenterZ=0 NormalX=0 NormalY=0 NormalZ=1 AngleXU=0 Radius=7.50003 StartAngle=3.14159 EndAngle=4.71239
    g3: ArcOfCircle CenterX=-7.50003 CenterY=-7.50003 CenterZ=0 NormalX=0 NormalY=0 NormalZ=1 AngleXU=0 Radius=7.50003 StartAngle=3.39099e-06 EndAngle=1.5708
  constraints (16):
    c: Equal(g3,g1)
    c: Equal(g1,g2)
    c: Equal(g2,g0)
    c: Vertical(g0,g2)
    c: Horizontal(g3,g0)
    c: Vertical(g1,g3)
    c: Horizontal(g1,g2)
    c: Coincident(g1,g2)
    c: Coincident(g0,g2)
    c: Coincident(g3,g0)
    c: Coincident(g3,g1)
    c: PointOnObject(g1,g-1)
    c: PointOnObject(g1,g-2)
    c: DistanceY(g0,g-1) = 7.5
    c: Vertical(g0,g0)
    c: Horizontal(g1,g1)
FEATURE [PartDesign::Pocket] router010  label="RoundOver2 006"
  BaseFeature = -> router004
  Direction = (-1,0,-2e-16)
  Length = 5
  Length2 = 5
  Placement = pos=(21,-33,23) rot=(1,0,0;1.5708rad)
  Profile = -> routerPattern010
  SideType = 2
  Suppressed = false
  Type = 1
  Type2 = 0
FEATURE [PartDesign::Body] Body004  label="Body, Frame003"
  AllowCompound = true
  Group = -> [Sketch008,Pad004,Frame45Cut003,routerPattern,router,routerPattern004,router004,routerPattern010,router010]
  Origin = -> Origin009
  Tip = -> router010
PROVENANCE & LICENSES
A FreeCAD (.FCStd) document from a public repository crawl; recipes are the document's own serialized feature recipes (and, for linked parts, companion documents' recipes).
License: mit.
